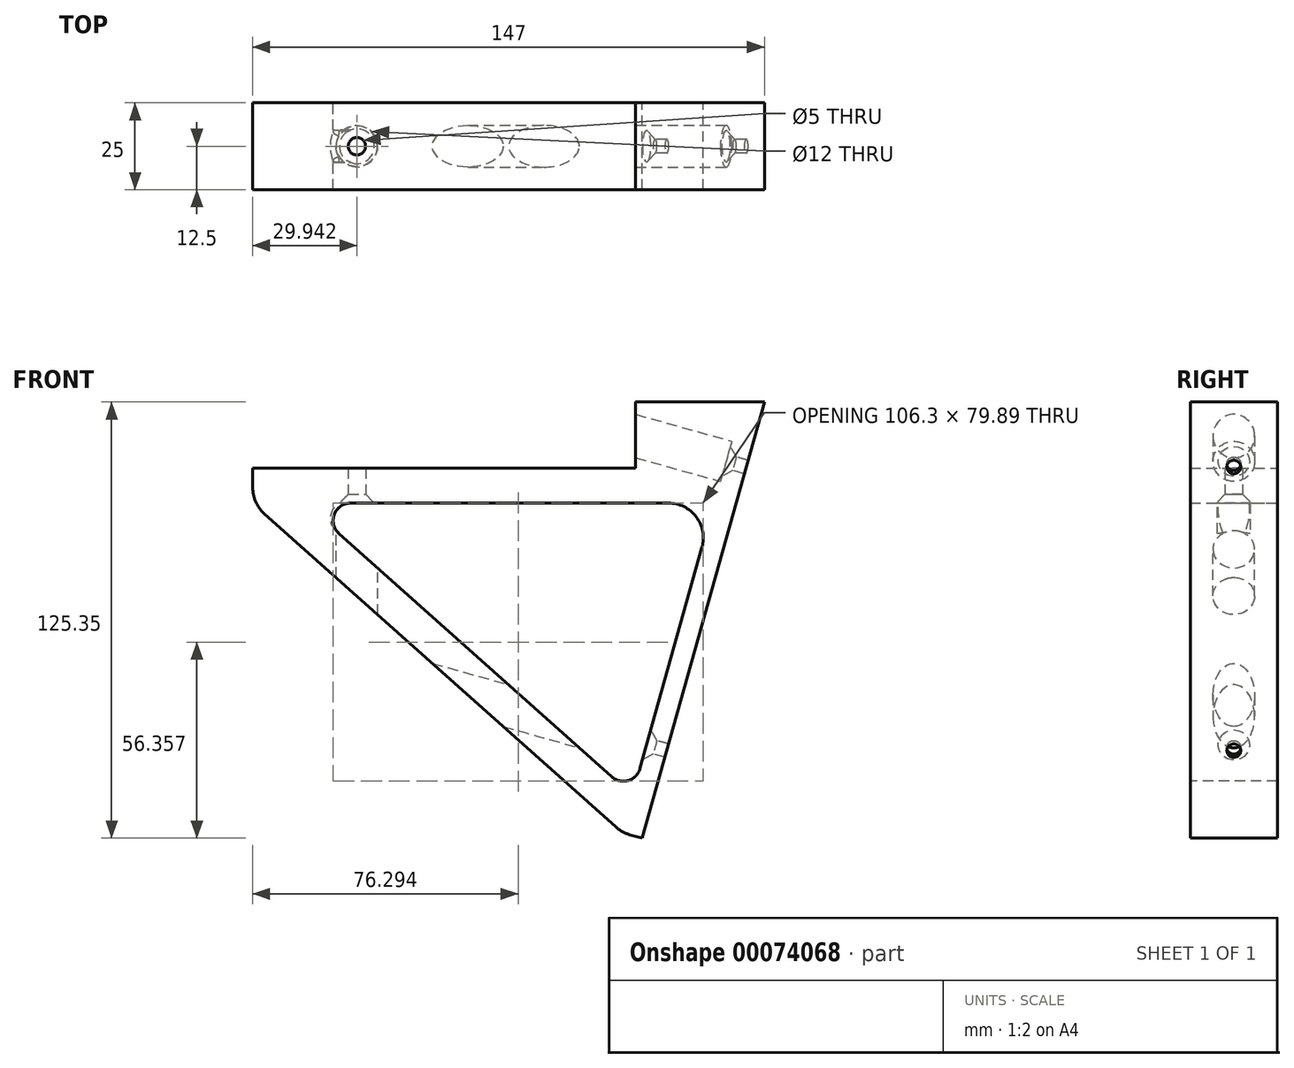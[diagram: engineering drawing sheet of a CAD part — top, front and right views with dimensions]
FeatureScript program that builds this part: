
annotation { "Feature Type Name" : "Feature", "Feature Type Description" : "" }
export const myFeature = defineFeature(function(context is Context, id is Id, definition is map)
    precondition{}
    {
        {
            var Q0;
            Q0=qCreatedBy(makeId("Front.planeOp"),FACE);
            var sketch = newSketch(context, id + "F0", { "sketchPlane" : qUnion([Q0])});
            skLineSegment(sketch, "E0", {"start": v(0, 0) * mm, "end": v(0, -132.14) * mm, "construction": true});
            skLineSegment(sketch, "E1", {"start": v(0, -132.14) * mm, "end": v(37, 0) * mm, "construction": true});
            skLineSegment(sketch, "E2", {"start": v(37, 0) * mm, "end": v(0, 0) * mm, "construction": true});
            skSolve(sketch);
        }
        {
            var Q0;
            Q0=qCreatedBy(makeId("Front.planeOp"),FACE);
            var sketch = newSketch(context, id + "F1", { "sketchPlane" : qUnion([Q0])});
            skLineSegment(sketch, "E3.0", {"start": v(37, 0) * mm, "end": v(0, 0) * mm});
            skLineSegment(sketch, "E4", {"start": v(0, 0) * mm, "end": v(0, -19.05) * mm});
            skLineSegment(sketch, "E5", {"start": v(0, -19.05) * mm, "end": v(-110, -19.05) * mm});
            skLineSegment(sketch, "E6", {"start": v(-110, -19.05) * mm, "end": v(-110, -29.05) * mm});
            skLineSegment(sketch, "E7", {"start": v(-110, -29.05) * mm, "end": v(28.87, -29.05) * mm});
            skLineSegment(sketch, "E8", {"start": v(28.87, -29.05) * mm, "end": v(37, 0) * mm});
            skLineSegment(sketch, "E9", {"start": v(28.87, -29.05) * mm, "end": v(1.9, -125.35) * mm});
            skLineSegment(sketch, "E10", {"start": v(1.9, -125.35) * mm, "end": v(-3.87, -123.73) * mm});
            skLineSegment(sketch, "E11", {"start": v(-3.87, -123.73) * mm, "end": v(22.64, -29.05) * mm});
            skLineSegment(sketch, "E12", {"start": v(22.64, -29.05) * mm, "end": v(28.87, -29.05) * mm});
            skLineSegment(sketch, "E13", {"start": v(-3.87, -123.73) * mm, "end": v(-110, -29.05) * mm});
            skLineSegment(sketch, "E14", {"start": v(-110, -29.05) * mm, "end": v(-94.98, -29.05) * mm});
            skLineSegment(sketch, "E15", {"start": v(-94.98, -29.05) * mm, "end": v(-0.87, -113) * mm});
            skLineSegment(sketch, "E16", {"start": v(-0.87, -113) * mm, "end": v(-3.87, -123.73) * mm});
            skSolve(sketch);
        }
        {
            var Q0;
            Q0=makeQuery(id+"F1.imprint","IMPRINT",FACE,{"disambiguationData":[TD([[makeQuery(id+"F1.imprint","IMPRINT",EDGE,{"derivedFrom":sQuery(id+"F1.wireOp",EDGE,"E3.0")}),1.0]])]});
            var Q1;
            Q1=makeQuery(id+"F1.imprint","IMPRINT",FACE,{"disambiguationData":[TD([[makeQuery(id+"F1.imprint","IMPRINT",EDGE,{"derivedFrom":sQuery(id+"F1.wireOp",EDGE,"E9")}),-1.0]])]});
            var Q2;
            Q2=makeQuery(id+"F1.imprint","IMPRINT",FACE,{"disambiguationData":[TD([[makeQuery(id+"F1.imprint","IMPRINT",EDGE,{"derivedFrom":sQuery(id+"F1.wireOp",EDGE,"E13")}),-1.0]])]});
            extrude(context, id + "F2", {"entities" : qUnion([Q0, Q1, Q2]), "endBound" : BoundingType.SYMMETRIC, "depth" : 25 * mm});
        }
        {
            var Q0;
            Q0=makeQuery(id+"F2.opExtrude","SWEPT_FACE",FACE,{"disambiguationData":[OSD([sQuery(id+"F1.wireOp",EDGE,"E11")])]});
            var sketch = newSketch(context, id + "F3", { "sketchPlane" : qUnion([Q0])});
            skLineSegment(sketch, "E17", {"start": v(0, -21.87) * mm, "end": v(0, -109.06) * mm, "construction": true});
            skPoint(sketch, "E18", {"position": v(0, -9.41) * mm});
            skPoint(sketch, "E19", {"position": v(0, -94.06) * mm});
            skCircle(sketch, "E20", {"center": v(0, -9.41) * mm, "radius": 6 * mm});
            skCircle(sketch, "E21", {"center": v(0, -94.06) * mm, "radius": 6 * mm});
            skSolve(sketch);
        }
        {
            var Q0;
            Q0=sQuery(id+"F3.wireOp",VERTEX,"E18");
            var Q1;
            Q1=sQuery(id+"F3.wireOp",VERTEX,"E19");
            var Q2;
            Q2=makeQuery(id+"F2.opExtrude","SWEPT_BODY",BODY,{"disambiguationData":[OSD([sQuery(id+"F1.wireOp",EDGE,"E3.0"),sQuery(id+"F1.wireOp",EDGE,"E4"),sQuery(id+"F1.wireOp",EDGE,"E5"),sQuery(id+"F1.wireOp",EDGE,"E6"),sQuery(id+"F1.wireOp",EDGE,"E7"),sQuery(id+"F1.wireOp",EDGE,"E8"),sQuery(id+"F1.wireOp",EDGE,"E9"),sQuery(id+"F1.wireOp",EDGE,"E10"),sQuery(id+"F1.wireOp",EDGE,"E11"),sQuery(id+"F1.wireOp",EDGE,"E13"),sQuery(id+"F1.wireOp",EDGE,"E15")])]});
            hole(context, id + "F4", {"style" : HoleStyle.C_SINK, "holeDiameter" : 4 * mm, "cSinkDiameter" : 9 * mm, "endStyle" : HoleEndStyle.THROUGH, "locations" : qUnion([Q0, Q1]), "scope" : qUnion([Q2]), "cSinkAngle" : 90 * degree});
        }
        {
            var Q0;
            Q0=makeQuery(id+"F3.imprint","IMPRINT",FACE,{"disambiguationData":[TD([[makeQuery(id+"F3.imprint","IMPRINT",EDGE,{"derivedFrom":sQuery(id+"F3.wireOp",EDGE,"E20")}),1.0]])]});
            var Q1;
            Q1=makeQuery(id+"F3.imprint","IMPRINT",FACE,{"disambiguationData":[TD([[makeQuery(id+"F3.imprint","IMPRINT",EDGE,{"derivedFrom":sQuery(id+"F3.wireOp",EDGE,"E21")}),1.0]])]});
            extrude(context, id + "F5", {"entities" : qUnion([Q0, Q1]), "operationType" : NewBodyOperationType.REMOVE, "endBound" : BoundingType.THROUGH_ALL, "depth" : 130.06 * mm});
        }
        {
            var Q0;
            Q0=makeQuery(id+"F2.opExtrude","SWEPT_FACE",FACE,{"disambiguationData":[OSD([sQuery(id+"F1.wireOp",EDGE,"E7")])]});
            var sketch = newSketch(context, id + "F6", { "sketchPlane" : qUnion([Q0])});
            skLineSegment(sketch, "E22", {"start": v(22.64, 0) * mm, "end": v(-94.98, 0) * mm, "construction": true});
            skPoint(sketch, "E23", {"position": v(-80.06, 0) * mm});
            skCircle(sketch, "E24", {"center": v(-80.06, 0) * mm, "radius": 6 * mm});
            skSolve(sketch);
        }
        {
            var Q0;
            Q0=sQuery(id+"F6.wireOp",VERTEX,"E24.center");
            var Q1;
            Q1=makeQuery(id+"F2.opExtrude","SWEPT_BODY",BODY,{"disambiguationData":[OSD([sQuery(id+"F1.wireOp",EDGE,"E3.0"),sQuery(id+"F1.wireOp",EDGE,"E4"),sQuery(id+"F1.wireOp",EDGE,"E5"),sQuery(id+"F1.wireOp",EDGE,"E6"),sQuery(id+"F1.wireOp",EDGE,"E7"),sQuery(id+"F1.wireOp",EDGE,"E8"),sQuery(id+"F1.wireOp",EDGE,"E9"),sQuery(id+"F1.wireOp",EDGE,"E10"),sQuery(id+"F1.wireOp",EDGE,"E11"),sQuery(id+"F1.wireOp",EDGE,"E13"),sQuery(id+"F1.wireOp",EDGE,"E15")])]});
            hole(context, id + "F7", {"style" : HoleStyle.C_SINK, "holeDiameter" : 5 * mm, "cSinkDiameter" : 10 * mm, "endStyle" : HoleEndStyle.THROUGH, "locations" : qUnion([Q0]), "scope" : qUnion([Q1]), "cSinkAngle" : 90 * degree});
        }
        {
            var Q0;
            Q0=makeQuery(id+"F6.imprint","IMPRINT",FACE,{"disambiguationData":[TD([[makeQuery(id+"F6.imprint","IMPRINT",EDGE,{"derivedFrom":sQuery(id+"F6.wireOp",EDGE,"E24")}),1.0]])]});
            extrude(context, id + "F8", {"entities" : qUnion([Q0]), "operationType" : NewBodyOperationType.REMOVE, "endBound" : BoundingType.THROUGH_ALL, "depth" : 25 * mm});
        }
        {
            var Q0;
            Q0=makeQuery(id+"F2.opExtrude","SWEPT_EDGE",EDGE,{"disambiguationData":[OSD([sQuery(id+"F1.wireOp",EDGE,"E6"),sQuery(id+"F1.wireOp",EDGE,"E13"),sQuery(id+"F1.wireOp",EDGE,"E14")])]});
            var Q1;
            Q1=makeQuery(id+"F2.opExtrude","SWEPT_EDGE",EDGE,{"disambiguationData":[OSD([sQuery(id+"F1.wireOp",EDGE,"E10"),sQuery(id+"F1.wireOp",EDGE,"E13"),sQuery(id+"F1.wireOp",EDGE,"E16")])]});
            var Q2;
            Q2=makeQuery(id+"F2.opExtrude","SWEPT_EDGE",EDGE,{"disambiguationData":[OSD([sQuery(id+"F1.wireOp",EDGE,"E7"),sQuery(id+"F1.wireOp",EDGE,"E11"),sQuery(id+"F1.wireOp",EDGE,"E12")])]});
            fillet(context, id + "F9", {"entities" : qUnion([Q0, Q1, Q2]), "radius" : 10 * mm, "tangentPropagation" : true, "allowEdgeOverflow" : false});
        }
        {
            var Q0;
            Q0=makeQuery(id+"F2.opExtrude","SWEPT_EDGE",EDGE,{"disambiguationData":[OSD([sQuery(id+"F1.wireOp",EDGE,"E7"),sQuery(id+"F1.wireOp",EDGE,"E14"),sQuery(id+"F1.wireOp",EDGE,"E15")])]});
            var Q1;
            Q1=makeQuery(id+"F2.opExtrude","SWEPT_EDGE",EDGE,{"disambiguationData":[OSD([sQuery(id+"F1.wireOp",EDGE,"E11"),sQuery(id+"F1.wireOp",EDGE,"E15"),sQuery(id+"F1.wireOp",EDGE,"E16")])]});
            fillet(context, id + "F10", {"entities" : qUnion([Q0, Q1]), "radius" : 5 * mm, "tangentPropagation" : true, "allowEdgeOverflow" : false});
        }
    });
